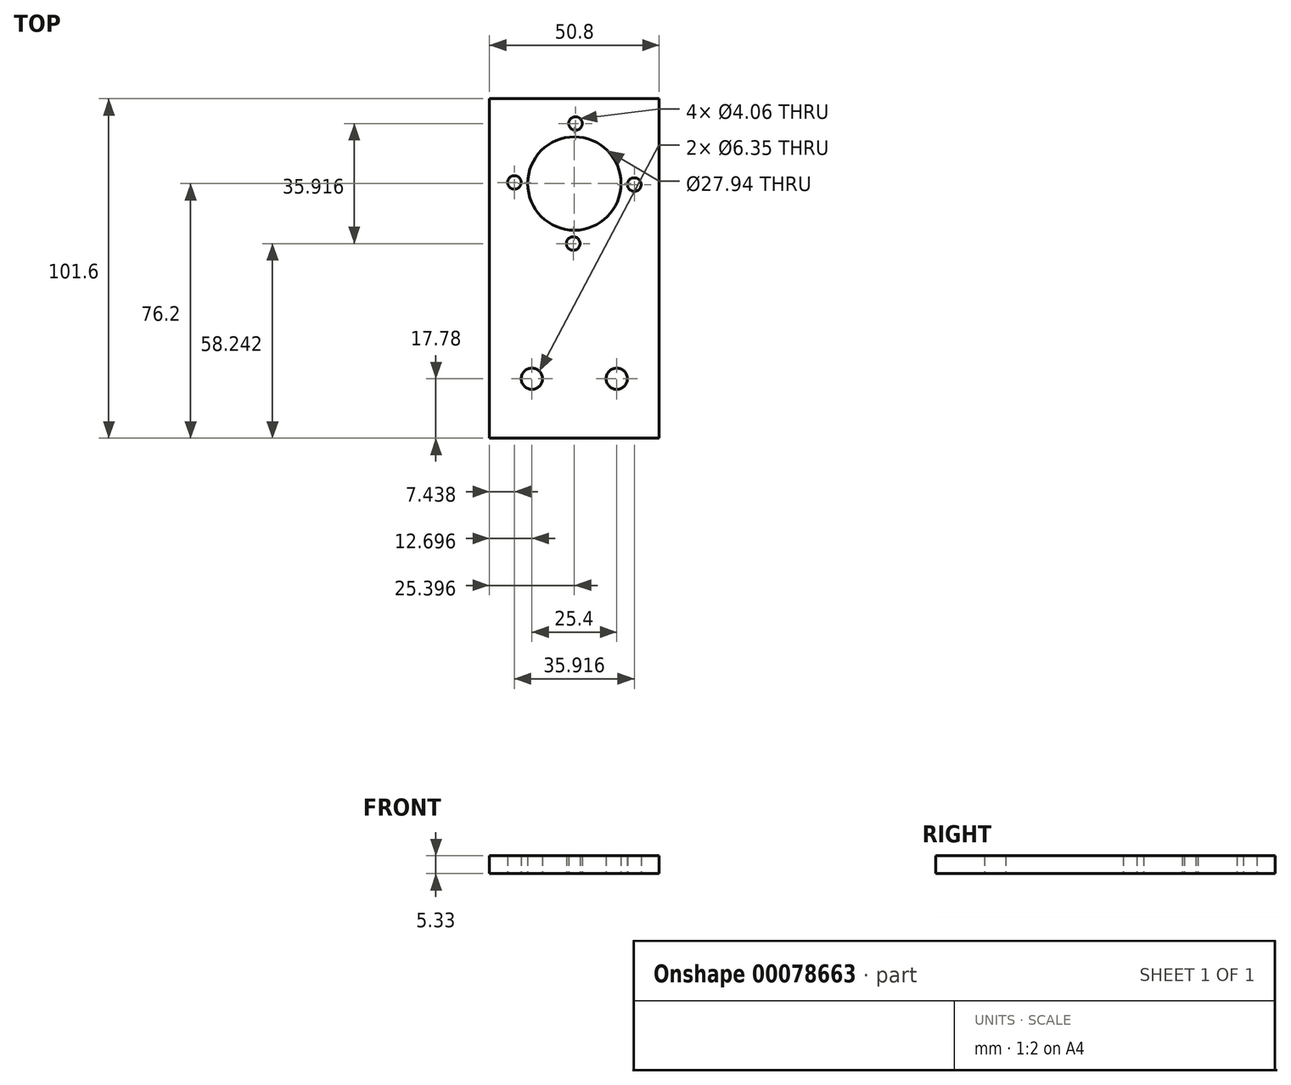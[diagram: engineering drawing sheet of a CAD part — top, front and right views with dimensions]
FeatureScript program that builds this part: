
annotation { "Feature Type Name" : "Feature", "Feature Type Description" : "" }
export const myFeature = defineFeature(function(context is Context, id is Id, definition is map)
    precondition{}
    {
        {
            var Q0;
            Q0=qCreatedBy(makeId("Top.planeOp"),FACE);
            var sketch = newSketch(context, id + "F0", { "sketchPlane" : qUnion([Q0])});
            skCircle(sketch, "E0", {"center": v(-17.73, 78.74) * mm, "radius": 2.03 * mm});
            skCircle(sketch, "E1.1.0", {"center": v(-36.01, 61.1) * mm, "radius": 2.03 * mm});
            skCircle(sketch, "E1.2.0", {"center": v(-18.38, 42.82) * mm, "radius": 2.03 * mm});
            skCircle(sketch, "E1.3.0", {"center": v(-0.1, 60.46) * mm, "radius": 2.03 * mm});
            skPoint(sketch, "E1.center", {"position": v(-18.05, 60.78) * mm});
            skCircle(sketch, "E2", {"center": v(-18.05, 60.78) * mm, "radius": 13.97 * mm});
            skLineSegment(sketch, "E3.top", {"start": v(7.35, 86.18) * mm, "end": v(-43.45, 86.18) * mm});
            skLineSegment(sketch, "E4.top", {"start": v(7.35, -15.42) * mm, "end": v(-43.45, -15.42) * mm});
            skLineSegment(sketch, "E5", {"start": v(7.35, 86.18) * mm, "end": v(7.35, -15.42) * mm});
            skLineSegment(sketch, "E6", {"start": v(-43.45, -15.42) * mm, "end": v(-43.45, 86.18) * mm});
            skCircle(sketch, "E7", {"center": v(-30.75, 2.36) * mm, "radius": 3.18 * mm});
            skCircle(sketch, "E8", {"center": v(-5.35, 2.36) * mm, "radius": 3.18 * mm});
            skSolve(sketch);
        }
        {
            var Q0;
            Q0=qSketchRegion(id+"F0",true);
            extrude(context, id + "F1", {"entities" : qUnion([Q0]), "depth" : 5.33 * mm});
        }
        {
            var Q0;
            Q0=makeQuery(id+"F1.opExtrude","CAP_FACE",FACE,{"disambiguationData":[OSD([sQuery(id+"F0.wireOp",EDGE,"E0"),sQuery(id+"F0.wireOp",EDGE,"E1.1.0"),sQuery(id+"F0.wireOp",EDGE,"E1.2.0"),sQuery(id+"F0.wireOp",EDGE,"E1.3.0"),sQuery(id+"F0.wireOp",EDGE,"E2"),sQuery(id+"F0.wireOp",EDGE,"E3.top"),sQuery(id+"F0.wireOp",EDGE,"E4.top"),sQuery(id+"F0.wireOp",EDGE,"E5"),sQuery(id+"F0.wireOp",EDGE,"E6")])],"isStart":true});
            var sketch = newSketch(context, id + "F2", { "sketchPlane" : qUnion([Q0])});
            skCircle(sketch, "E9", {"center": v(-5.35, -2.36) * mm, "radius": 3.18 * mm});
            skCircle(sketch, "E10", {"center": v(-30.75, -2.36) * mm, "radius": 3.18 * mm});
            skSolve(sketch);
        }
        {
            var Q0;
            Q0=qSketchRegion(id+"F2",true);
            extrude(context, id + "F3", {"entities" : qUnion([Q0]), "operationType" : NewBodyOperationType.REMOVE, "oppositeDirection" : true, "depth" : 25.4 * mm});
        }
    });
